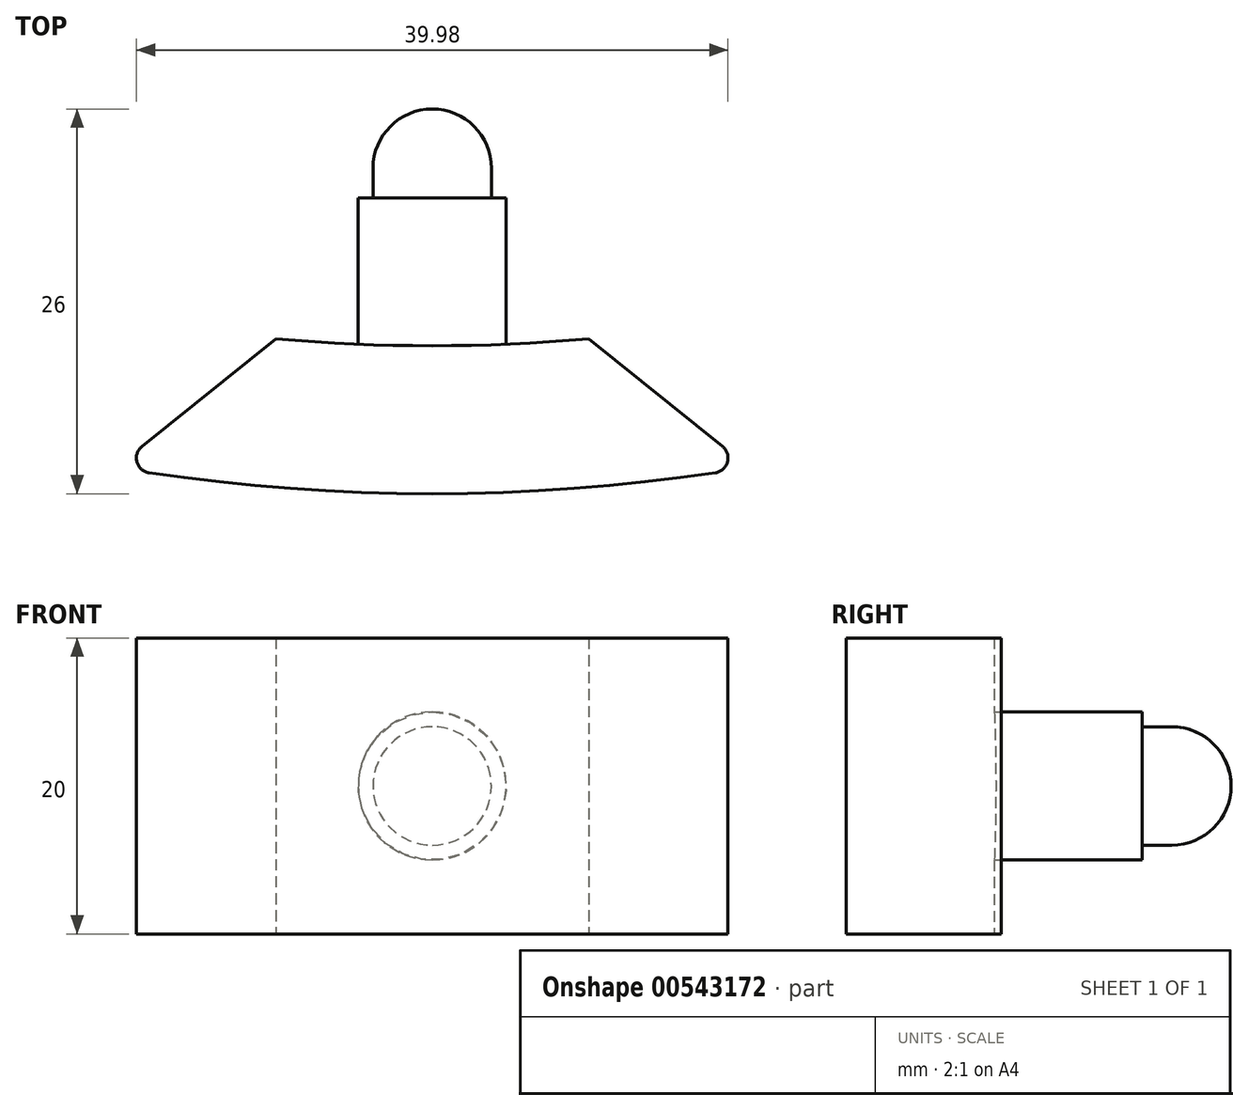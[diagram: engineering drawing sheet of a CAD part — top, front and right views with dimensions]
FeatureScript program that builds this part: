
annotation { "Feature Type Name" : "Feature", "Feature Type Description" : "" }
export const myFeature = defineFeature(function(context is Context, id is Id, definition is map)
    precondition{}
    {
        {
            var Q0;
            Q0=qCreatedBy(makeId("Front.planeOp"),FACE);
            var sketch = newSketch(context, id + "F0", { "sketchPlane" : qUnion([Q0])});
            skCircle(sketch, "E0", {"center": v(0, 0) * mm, "radius": 5 * mm});
            skSolve(sketch);
        }
        {
            var Q0;
            Q0 = qSketchRegion(id + "F0", true);
            extrude(context, id + "F1", {"entities" : qUnion([Q0]), "depth" : 10 * mm, "offsetDistance" : 25 * mm});
        }
        {
            var Q0;
            Q0=makeQuery(id+"F1.opExtrude","CAP_FACE",FACE,{"disambiguationData":[OSD([sQuery(id+"F0.wireOp",EDGE,"E0")])],"isStart":true});
            var sketch = newSketch(context, id + "F2", { "sketchPlane" : qUnion([Q0])});
            skCircle(sketch, "E1", {"center": v(0, 0) * mm, "radius": 4 * mm});
            skSolve(sketch);
        }
        {
            var Q0;
            Q0 = qSketchRegion(id + "F2", true);
            extrude(context, id + "F3", {"entities" : qUnion([Q0]), "operationType" : NewBodyOperationType.ADD, "depth" : 6 * mm, "offsetDistance" : 25 * mm});
        }
        {
            var Q0;
            Q0=makeQuery(id+"F3.opExtrude","CAP_EDGE",EDGE,{"disambiguationData":[OSD([sQuery(id+"F2.wireOp",EDGE,"E1")])],"isStart":false});
            fillet(context, id + "F4", {"entities" : qUnion([Q0]), "radius" : 4 * mm, "tangentPropagation" : true, "allowEdgeOverflow" : false});
        }
        {
            var Q0;
            Q0=qCreatedBy(makeId("Top.planeOp"),FACE);
            var sketch = newSketch(context, id + "F5", { "sketchPlane" : qUnion([Q0])});
            skArc(sketch, "E2", {"start": v(-10.46, -9.54) * mm, "mid": v(0, -10) * mm, "end": v(10.46, -9.54) * mm});
            skArc(sketch, "E3", {"start": v(-21.7, -13.1) * mm, "mid": v(-16.32, -13.93) * mm, "end": v(-10.9, -14.52) * mm});
            skLineSegment(sketch, "E4", {"start": v(0, 110) * mm, "end": v(-20.84, -8.18) * mm, "construction": true});
            skLineSegment(sketch, "E5", {"start": v(-20.22, -4.66) * mm, "end": v(-22.57, -18.03) * mm, "construction": true});
            skLineSegment(sketch, "E6", {"start": v(0, 110) * mm, "end": v(20.84, -8.18) * mm, "construction": true});
            skLineSegment(sketch, "E7", {"start": v(20.4, -5.7) * mm, "end": v(22.57, -18.03) * mm, "construction": true});
            skLineSegment(sketch, "E8", {"start": v(-20.84, -8.18) * mm, "end": v(-21.7, -13.1) * mm});
            skLineSegment(sketch, "E9", {"start": v(20.84, -8.18) * mm, "end": v(21.7, -13.1) * mm});
            skArc(sketch, "E10", {"start": v(-22.57, -18.03) * mm, "mid": v(0, -20) * mm, "end": v(22.57, -18.03) * mm});
            skLineSegment(sketch, "E11", {"start": v(0, 110) * mm, "end": v(-10.9, -14.52) * mm, "construction": true});
            skLineSegment(sketch, "E12", {"start": v(0, 110) * mm, "end": v(10.9, -14.52) * mm, "construction": true});
            skArc(sketch, "E13.trimOffspring", {"start": v(10.9, -14.52) * mm, "mid": v(16.32, -13.93) * mm, "end": v(21.7, -13.1) * mm});
            skLineSegment(sketch, "E14", {"start": v(-22.57, -18.03) * mm, "end": v(-21.7, -13.1) * mm});
            skLineSegment(sketch, "E15", {"start": v(22.57, -18.03) * mm, "end": v(21.7, -13.1) * mm});
            skLineSegment(sketch, "E16", {"start": v(-10.9, -14.52) * mm, "end": v(-10.46, -9.54) * mm});
            skLineSegment(sketch, "E17", {"start": v(10.9, -14.52) * mm, "end": v(10.46, -9.54) * mm});
            skSolve(sketch);
        }
        {
            var Q0;
            Q0 = qSketchRegion(id + "F5", true);
            extrude(context, id + "F6", {"entities" : qUnion([Q0]), "operationType" : NewBodyOperationType.ADD, "depth" : 10 * mm, "offsetDistance" : 25 * mm, "hasSecondDirection" : true, "secondDirectionOppositeDirection" : true, "secondDirectionDepth" : 10 * mm});
        }
        {
            var Q0;
            Q0=makeQuery(id+"F6.opExtrude","SWEPT_EDGE",EDGE,{"disambiguationData":[OSD([sQuery(id+"F5.wireOp",EDGE,"E3"),sQuery(id+"F5.wireOp",EDGE,"E16")])]});
            var Q1;
            Q1=makeQuery(id+"F6.opExtrude","SWEPT_EDGE",EDGE,{"disambiguationData":[OSD([sQuery(id+"F5.wireOp",EDGE,"E13.trimOffspring"),sQuery(id+"F5.wireOp",EDGE,"E17")])]});
            chamfer(context, id + "F7", {"entities" : qUnion([Q0, Q1]), "chamferType" : ChamferType.OFFSET_ANGLE, "width" : 5 * mm, "oppositeDirection" : true, "angle" : 45 * degree, "tangentPropagation" : true});
        }
        {
            var Q0;
            Q0=makeQuery(id+"F6.opExtrude","CAP_FACE",FACE,{"disambiguationData":[OSD([sQuery(id+"F5.wireOp",EDGE,"E2"),sQuery(id+"F5.wireOp",EDGE,"E3"),sQuery(id+"F5.wireOp",EDGE,"E10"),sQuery(id+"F5.wireOp",EDGE,"E13.trimOffspring"),sQuery(id+"F5.wireOp",EDGE,"E14"),sQuery(id+"F5.wireOp",EDGE,"E15"),sQuery(id+"F5.wireOp",EDGE,"E16"),sQuery(id+"F5.wireOp",EDGE,"E17")])],"isStart":false});
            var sketch = newSketch(context, id + "F8", { "sketchPlane" : qUnion([Q0])});
            skLineSegment(sketch, "E18", {"start": v(-16.07, -13.96) * mm, "end": v(-22.14, -18.84) * mm});
            skPoint(sketch, "E18.endSnap0", {"position": v(-22.14, -15.56) * mm});
            skLineSegment(sketch, "E19", {"start": v(-22.14, -18.84) * mm, "end": v(-26.21, -18.84) * mm});
            skLineSegment(sketch, "E20", {"start": v(-26.21, -18.84) * mm, "end": v(-26.21, -8.74) * mm});
            skLineSegment(sketch, "E21", {"start": v(-26.21, -8.74) * mm, "end": v(-16.07, -13.96) * mm});
            skPoint(sketch, "E22.MirrorP", {"position": v(22.14, -15.56) * mm});
            skLineSegment(sketch, "E23.MirrorCS", {"start": v(16.07, -13.96) * mm, "end": v(22.14, -18.84) * mm});
            skLineSegment(sketch, "E24.MirrorCS", {"start": v(22.14, -18.84) * mm, "end": v(26.21, -18.84) * mm});
            skLineSegment(sketch, "E25.MirrorCS", {"start": v(26.21, -18.84) * mm, "end": v(26.21, -8.74) * mm});
            skLineSegment(sketch, "E26.MirrorCS", {"start": v(26.21, -8.74) * mm, "end": v(16.07, -13.96) * mm});
            skSolve(sketch);
        }
        {
            var Q0;
            Q0 = qSketchRegion(id + "F8", true);
            extrude(context, id + "F9", {"entities" : qUnion([Q0]), "operationType" : NewBodyOperationType.REMOVE, "oppositeDirection" : true, "depth" : 25 * mm, "offsetDistance" : 25 * mm});
        }
        {
            var Q0;
            Q0=makeQuery(id+"F9.boolean.opBoolean","INTERSECT",EDGE,{"derivedFrom":[makeQuery(id+"F6.opExtrude","SWEPT_FACE",FACE,{"disambiguationData":[OSD([sQuery(id+"F5.wireOp",EDGE,"E10")])]}),makeQuery(id+"F9.opExtrude","SWEPT_FACE",FACE,{"disambiguationData":[OSD([sQuery(id+"F8.wireOp",EDGE,"E18")])]})]});
            var Q1;
            Q1=makeQuery(id+"F9.boolean.opBoolean","INTERSECT",EDGE,{"derivedFrom":[makeQuery(id+"F6.opExtrude","SWEPT_FACE",FACE,{"disambiguationData":[OSD([sQuery(id+"F5.wireOp",EDGE,"E10")])]}),makeQuery(id+"F9.opExtrude","SWEPT_FACE",FACE,{"disambiguationData":[OSD([sQuery(id+"F8.wireOp",EDGE,"E23.MirrorCS")])]})]});
            fillet(context, id + "F10", {"entities" : qUnion([Q0, Q1]), "radius" : 1 * mm, "tangentPropagation" : true, "allowEdgeOverflow" : false});
        }
    });
